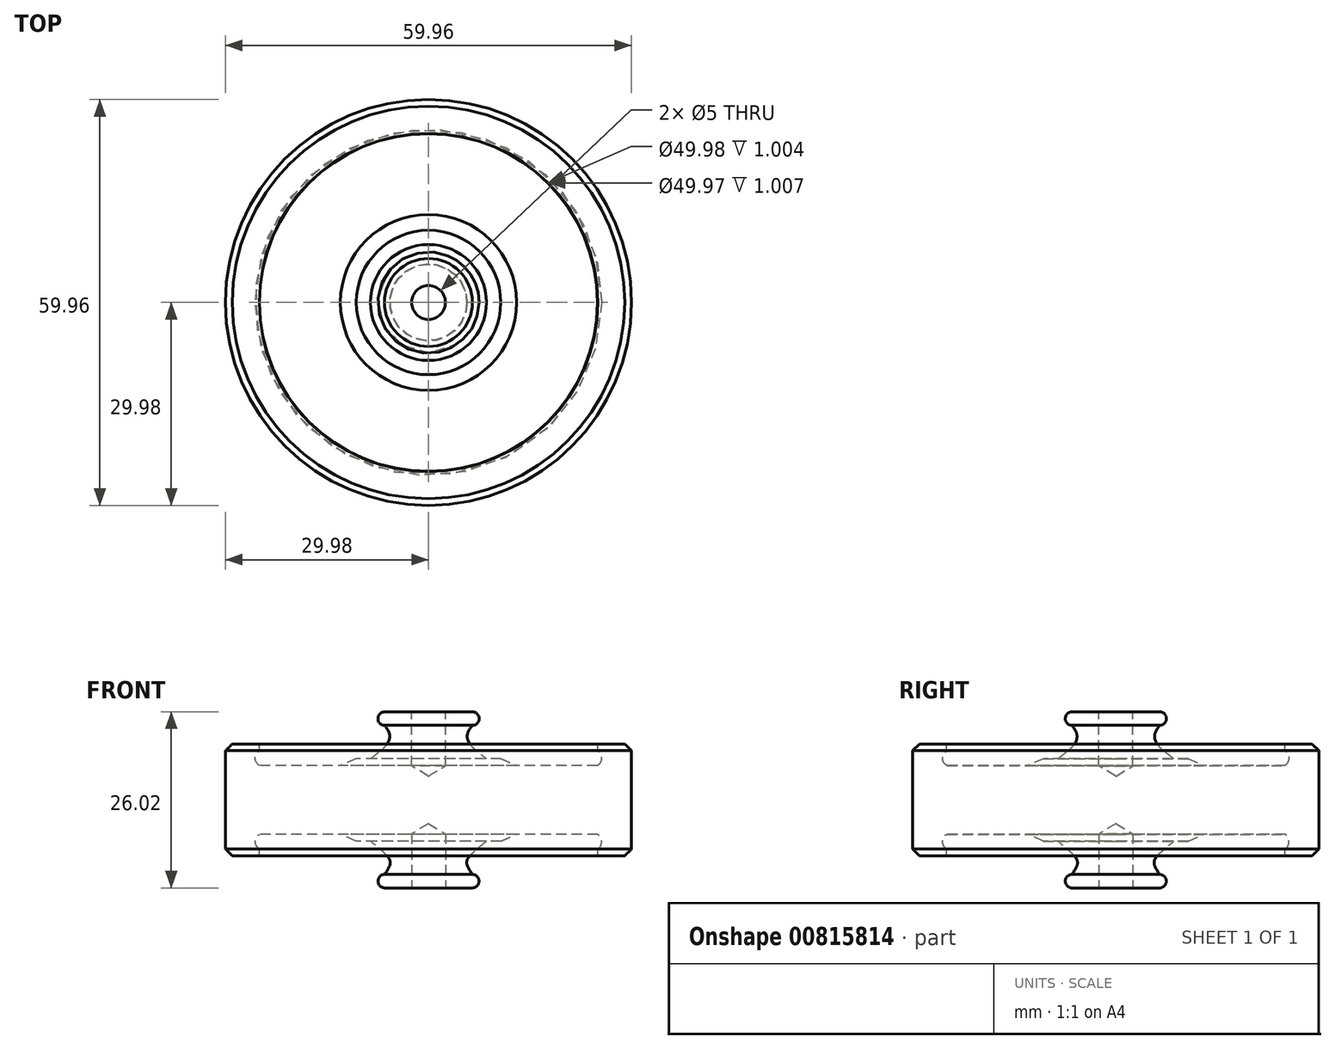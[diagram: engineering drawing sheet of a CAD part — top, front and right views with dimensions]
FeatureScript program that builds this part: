
annotation { "Feature Type Name" : "Feature", "Feature Type Description" : "" }
export const myFeature = defineFeature(function(context is Context, id is Id, definition is map)
    precondition{}
    {
        {
            var Q0;
            Q0=qCreatedBy(makeId("Right.planeOp"),FACE);
            var sketch = newSketch(context, id + "F0", { "sketchPlane" : qUnion([Q0])});
            skPoint(sketch, "E0", {"position": v(-6.5, 13) * mm});
            skLineSegment(sketch, "E1", {"start": v(-6.5, 13) * mm, "end": v(0, 13) * mm});
            skLineSegment(sketch, "E2", {"start": v(0, 13) * mm, "end": v(0, -13.01) * mm});
            skLineSegment(sketch, "E3", {"start": v(0, -13.01) * mm, "end": v(-6.5, -13.01) * mm});
            skPoint(sketch, "E4", {"position": v(-8.56, -6.11) * mm});
            skLineSegment(sketch, "E5", {"start": v(-8.56, -6.11) * mm, "end": v(-10.7, -6.11) * mm});
            skLineSegment(sketch, "E6", {"start": v(-10.7, -6.11) * mm, "end": v(-12.99, -5.08) * mm});
            skLineSegment(sketch, "E7", {"start": v(-12.99, -5.08) * mm, "end": v(-24.96, -5.08) * mm});
            skLineSegment(sketch, "E8", {"start": v(-24.99, -7.26) * mm, "end": v(-24.99, -8.27) * mm});
            skLineSegment(sketch, "E9", {"start": v(-24.99, -8.27) * mm, "end": v(-29.98, -8.27) * mm});
            skLineSegment(sketch, "E10", {"start": v(-29.98, -8.27) * mm, "end": v(-29.98, 8.25) * mm});
            skLineSegment(sketch, "E11", {"start": v(-29.98, 8.25) * mm, "end": v(-24.99, 8.25) * mm});
            skLineSegment(sketch, "E12", {"start": v(-24.99, 8.25) * mm, "end": v(-24.99, 7.25) * mm});
            skLineSegment(sketch, "E13", {"start": v(-8.56, 6.1) * mm, "end": v(-10.67, 6.1) * mm});
            skLineSegment(sketch, "E14", {"start": v(-10.67, 6.1) * mm, "end": v(-13, 5.07) * mm});
            skLineSegment(sketch, "E15", {"start": v(-13, 5.07) * mm, "end": v(-24.94, 5.07) * mm});
            skArc(sketch, "E16", {"start": v(-24.99, 7.25) * mm, "mid": v(-25.6, 6.15) * mm, "end": v(-24.94, 5.07) * mm});
            skArc(sketch, "E17", {"start": v(-24.96, -5.08) * mm, "mid": v(-25.58, -6.16) * mm, "end": v(-24.99, -7.26) * mm});
            skFitSpline(sketch, "E18", {"points": [v(-8.56, -6.11) * mm, v(-6.03, -8.37) * mm, v(-5.66, -9.12) * mm, v(-5.76, -9.8) * mm, v(-6.48, -11) * mm], "startDerivative": vector(7.97, -6.52) * mm, "endDerivative": vector(-3.46, -5.08) * mm});
            skArc(sketch, "E19", {"start": v(-6.48, -11) * mm, "mid": v(-7.46, -12) * mm, "end": v(-6.5, -13.01) * mm});
            skArc(sketch, "E20", {"start": v(-6.5, 13) * mm, "mid": v(-7.47, 12) * mm, "end": v(-6.5, 11) * mm});
            skFitSpline(sketch, "E21", {"points": [v(-6.5, 11) * mm, v(-5.77, 9.8) * mm, v(-6.05, 8.36) * mm, v(-8.56, 6.1) * mm], "startDerivative": vector(3.25, -4.1) * mm, "endDerivative": vector(-7.06, -5.16) * mm});
            skSolve(sketch);
        }
        {
            var Q0;
            Q0=makeQuery(id+"F0.imprint","IMPRINT",FACE,{"disambiguationData":[TD([[makeQuery(id+"F0.imprint","IMPRINT",EDGE,{"derivedFrom":sQuery(id+"F0.wireOp",EDGE,"E1")}),-1.0]])]});
            var Q1;
            {var subQ0=sQuery(id+"FqgRLvqQ2pUCHxM_0.wireOp",EDGE,"18cebc9b-4070-4290-8cd6-7f4f885b17936.MirrorCS");var subQ1=sQuery(id+"FqgRLvqQ2pUCHxM_0.wireOp",EDGE,"18cebc9b-4070-4290-8cd6-7f4f885b17932.MirrorCS");var subQ2=makeQuery(id+"FqgRLvqQ2pUCHxM_0.imprint","INTERSECT",VERTEX,{"disambiguationData":[OD(0.0)],"derivedFrom":[subQ1,subQ0]});Q1=makeQuery(id+"FqgRLvqQ2pUCHxM_0.imprint","IMPRINT",FACE,{"disambiguationData":[TD([[makeQuery(id+"FqgRLvqQ2pUCHxM_0.imprint","IMPRINT",EDGE,{"disambiguationData":[TD([[subQ2,-1.0]])],"derivedFrom":subQ1}),-1.0]])]});}
            var Q2;
            Q2=sQuery(id+"F0.wireOp",EDGE,"E2");
            revolve(context, id + "F1", {"surfaceOperationType" : NewSurfaceOperationType.NEW, "entities" : qUnion([Q0, Q1]), "axis" : qUnion([Q2]), "revolveType" : RevolveType.FULL});
        }
        {
            var Q0;
            Q0=makeQuery(id+"F1.opRevolve","SWEPT_EDGE",EDGE,{"disambiguationData":[OSD([sQuery(id+"F0.wireOp",EDGE,"E10"),sQuery(id+"F0.wireOp",EDGE,"E11")])]});
            var Q1;
            Q1=makeQuery(id+"F1.opRevolve","SWEPT_EDGE",EDGE,{"disambiguationData":[OSD([sQuery(id+"F0.wireOp",EDGE,"E9"),sQuery(id+"F0.wireOp",EDGE,"E10")])]});
            chamfer(context, id + "F2", {"entities" : qUnion([Q0, Q1]), "width" : 1 * mm, "tangentPropagation" : true});
        }
        {
            var Q0;
            Q0=makeQuery(id+"F1.opRevolve","SWEPT_FACE",FACE,{"disambiguationData":[OSD([sQuery(id+"F0.wireOp",EDGE,"E1")])]});
            var sketch = newSketch(context, id + "F3", { "sketchPlane" : qUnion([Q0])});
            skCircle(sketch, "E22", {"center": v(0, 0) * mm, "radius": 2.5 * mm});
            skSolve(sketch);
        }
        {
            var Q0;
            Q0=sQuery(id+"F3.wireOp",VERTEX,"E22.center");
            var Q1;
            Q1=makeQuery(id+"F1.opRevolve","SWEPT_BODY",BODY,{"disambiguationData":[OSD([sQuery(id+"F0.wireOp",EDGE,"E1"),sQuery(id+"F0.wireOp",EDGE,"E2"),sQuery(id+"F0.wireOp",EDGE,"E3"),sQuery(id+"F0.wireOp",EDGE,"E5"),sQuery(id+"F0.wireOp",EDGE,"E6"),sQuery(id+"F0.wireOp",EDGE,"E7"),sQuery(id+"F0.wireOp",EDGE,"E8"),sQuery(id+"F0.wireOp",EDGE,"E9"),sQuery(id+"F0.wireOp",EDGE,"E10"),sQuery(id+"F0.wireOp",EDGE,"E11"),sQuery(id+"F0.wireOp",EDGE,"E12"),sQuery(id+"F0.wireOp",EDGE,"E13"),sQuery(id+"F0.wireOp",EDGE,"E14"),sQuery(id+"F0.wireOp",EDGE,"E15"),sQuery(id+"F0.wireOp",EDGE,"E16"),sQuery(id+"F0.wireOp",EDGE,"E17"),sQuery(id+"F0.wireOp",EDGE,"E18"),sQuery(id+"F0.wireOp",EDGE,"E19"),sQuery(id+"F0.wireOp",EDGE,"E20"),sQuery(id+"F0.wireOp",EDGE,"E21")])]});
            hole(context, id + "F4", {"style" : HoleStyle.SIMPLE, "endStyle" : HoleEndStyle.BLIND, "standardTappedOrClearance" : lookupTablePath({ "standard" : "ISO", "engagement" : "75%", "pitch" : "1 mm", "size" : "M6", "type" : "Tapped" }), "standardBlindInLast" : lookupTablePath({ "standard" : "ISO", "engagement" : "75%", "pitch" : "1 mm", "size" : "M6", "type" : "Tapped" }), "holeDiameter" : 5 * mm, "majorDiameter" : 6 * mm, "showTappedDepth" : true, "holeDepth" : 8 * mm, "isTappedThrough" : true, "tappedDepth" : 5 * mm, "tapClearance" : 3, "locations" : qUnion([Q0]), "scope" : qUnion([Q1])});
        }
        {
            var Q0;
            Q0=makeQuery(id+"F1.opRevolve","SWEPT_FACE",FACE,{"disambiguationData":[OSD([sQuery(id+"F0.wireOp",EDGE,"E3")])]});
            var sketch = newSketch(context, id + "F5", { "sketchPlane" : qUnion([Q0])});
            skCircle(sketch, "E23", {"center": v(0, 0) * mm, "radius": 2.5 * mm});
            skSolve(sketch);
        }
        {
            var Q0;
            Q0=sQuery(id+"F5.wireOp",VERTEX,"E23.center");
            var Q1;
            Q1=makeQuery(id+"F1.opRevolve","SWEPT_BODY",BODY,{"disambiguationData":[OSD([sQuery(id+"F0.wireOp",EDGE,"E1"),sQuery(id+"F0.wireOp",EDGE,"E2"),sQuery(id+"F0.wireOp",EDGE,"E3"),sQuery(id+"F0.wireOp",EDGE,"E5"),sQuery(id+"F0.wireOp",EDGE,"E6"),sQuery(id+"F0.wireOp",EDGE,"E7"),sQuery(id+"F0.wireOp",EDGE,"E8"),sQuery(id+"F0.wireOp",EDGE,"E9"),sQuery(id+"F0.wireOp",EDGE,"E10"),sQuery(id+"F0.wireOp",EDGE,"E11"),sQuery(id+"F0.wireOp",EDGE,"E12"),sQuery(id+"F0.wireOp",EDGE,"E13"),sQuery(id+"F0.wireOp",EDGE,"E14"),sQuery(id+"F0.wireOp",EDGE,"E15"),sQuery(id+"F0.wireOp",EDGE,"E16"),sQuery(id+"F0.wireOp",EDGE,"E17"),sQuery(id+"F0.wireOp",EDGE,"E18"),sQuery(id+"F0.wireOp",EDGE,"E19"),sQuery(id+"F0.wireOp",EDGE,"E20"),sQuery(id+"F0.wireOp",EDGE,"E21")])]});
            hole(context, id + "F6", {"style" : HoleStyle.SIMPLE, "endStyle" : HoleEndStyle.BLIND, "standardTappedOrClearance" : lookupTablePath({ "standard" : "ISO", "engagement" : "75%", "pitch" : "1 mm", "size" : "M6", "type" : "Tapped" }), "standardBlindInLast" : lookupTablePath({ "standard" : "ISO", "engagement" : "75%", "pitch" : "1 mm", "size" : "M6", "type" : "Tapped" }), "holeDiameter" : 5 * mm, "majorDiameter" : 6 * mm, "showTappedDepth" : true, "holeDepth" : 8 * mm, "isTappedThrough" : true, "tappedDepth" : 5 * mm, "tapClearance" : 3, "locations" : qUnion([Q0]), "scope" : qUnion([Q1])});
        }
    });
